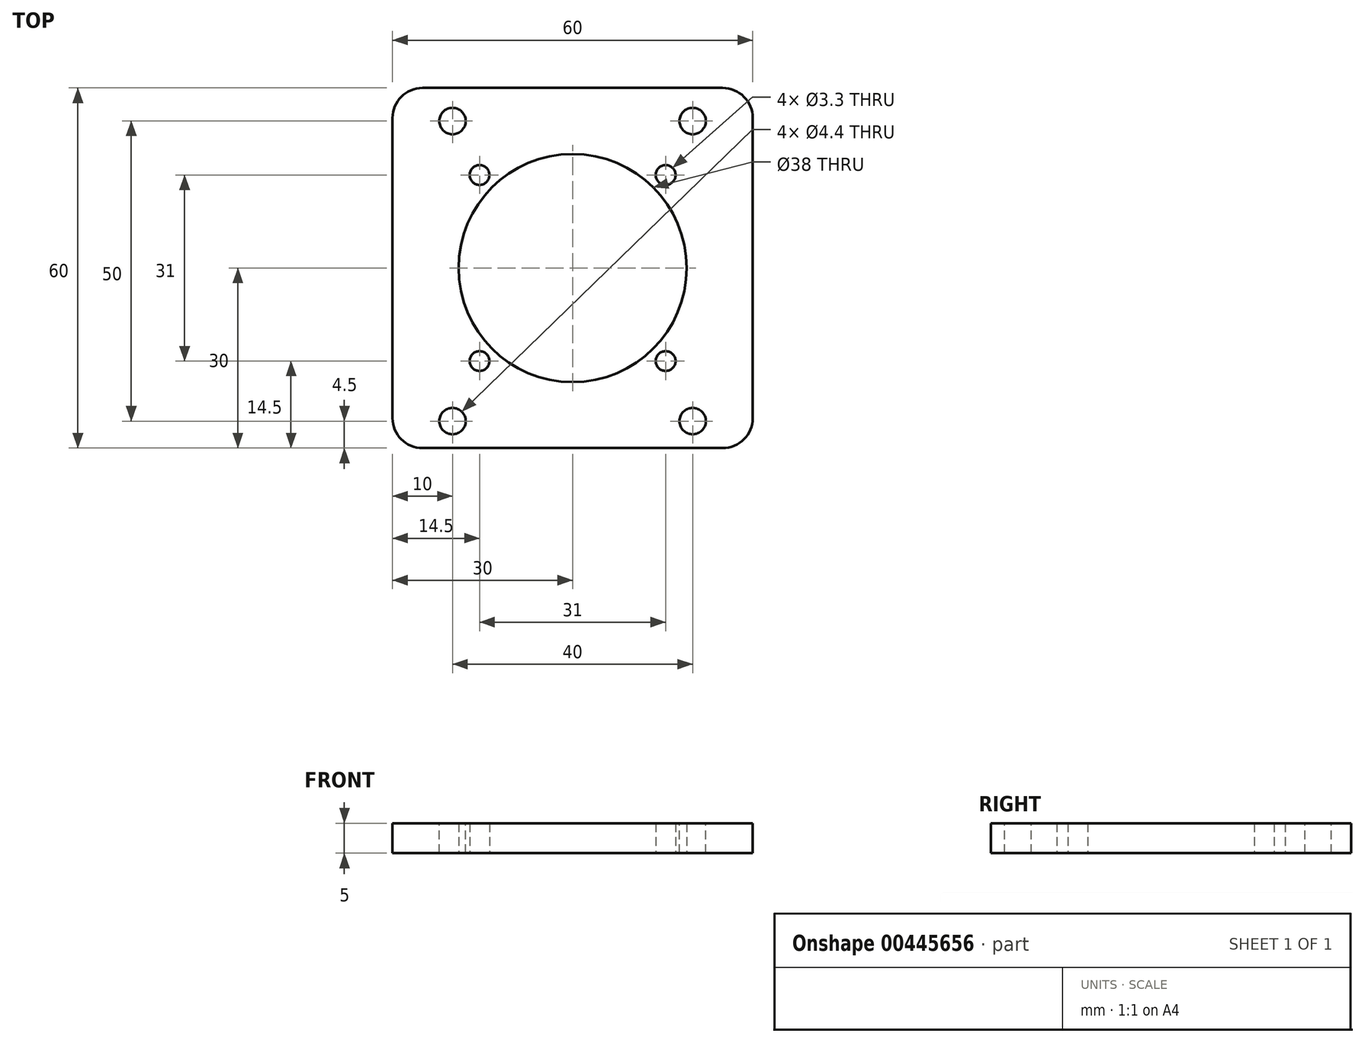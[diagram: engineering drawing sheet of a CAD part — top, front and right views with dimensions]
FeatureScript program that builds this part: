
annotation { "Feature Type Name" : "Feature", "Feature Type Description" : "" }
export const myFeature = defineFeature(function(context is Context, id is Id, definition is map)
    precondition{}
    {
        {
            var Q0;
            Q0=qCreatedBy(makeId("Top.planeOp"),FACE);
            var sketch = newSketch(context, id + "F0", { "sketchPlane" : qUnion([Q0])});
            skLineSegment(sketch, "E0.bottom", {"start": v(30, 30) * mm, "end": v(-30, 30) * mm});
            skLineSegment(sketch, "E0.top", {"start": v(30, -30) * mm, "end": v(-30, -30) * mm});
            skLineSegment(sketch, "E0.left", {"start": v(30, 30) * mm, "end": v(30, -30) * mm});
            skLineSegment(sketch, "E0.right", {"start": v(-30, 30) * mm, "end": v(-30, -30) * mm});
            skPoint(sketch, "E0.middle", {"position": v(0, 0) * mm});
            skCircle(sketch, "E1", {"center": v(0, 0) * mm, "radius": 19 * mm});
            skLineSegment(sketch, "E2.bottom", {"start": v(-15.5, 15.5) * mm, "end": v(15.5, 15.5) * mm, "construction": true});
            skLineSegment(sketch, "E2.top", {"start": v(-15.5, -15.5) * mm, "end": v(15.5, -15.5) * mm, "construction": true});
            skLineSegment(sketch, "E2.left", {"start": v(-15.5, 15.5) * mm, "end": v(-15.5, -15.5) * mm, "construction": true});
            skLineSegment(sketch, "E2.right", {"start": v(15.5, 15.5) * mm, "end": v(15.5, -15.5) * mm, "construction": true});
            skSolve(sketch);
        }
        {
            var Q0;
            Q0=qSketchRegion(id+"F0",true);
            extrude(context, id + "F1", {"entities" : qUnion([Q0]), "depth" : 5 * mm});
        }
        {
            var Q0;
            Q0=sQuery(id+"F0.wireOp",VERTEX,"E2.left.start");
            var Q1;
            Q1=sQuery(id+"F0.wireOp",VERTEX,"E2.right.start");
            var Q2;
            Q2=sQuery(id+"F0.wireOp",VERTEX,"E2.right.end");
            var Q3;
            Q3=sQuery(id+"F0.wireOp",VERTEX,"E2.left.end");
            var Q4;
            Q4=makeQuery(id+"F1.opExtrude","SWEPT_BODY",BODY,{"disambiguationData":[OSD([sQuery(id+"F0.wireOp",EDGE,"E0.bottom"),sQuery(id+"F0.wireOp",EDGE,"E0.top"),sQuery(id+"F0.wireOp",EDGE,"E0.left"),sQuery(id+"F0.wireOp",EDGE,"E0.right"),sQuery(id+"F0.wireOp",EDGE,"E1")])]});
            hole(context, id + "F2", {"style" : HoleStyle.SIMPLE, "endStyle" : HoleEndStyle.BLIND, "oppositeDirection" : true, "standardTappedOrClearance" : lookupTablePath({ "standard" : "ISO", "fit" : "Normal", "size" : "M3", "type" : "Clearance" }), "standardBlindInLast" : lookupTablePath({ "fit" : "Standard", "standard" : "ISO", "size" : "M3", "type" : "Clearance" }), "holeDiameter" : 3.3 * mm, "holeDepth" : 13.8 * mm, "tappedDepth" : 12 * mm, "tapClearance" : 3, "locations" : qUnion([Q0, Q1, Q2, Q3]), "scope" : qUnion([Q4])});
        }
        {
            var Q0;
            Q0=makeQuery(id+"F1.opExtrude","CAP_FACE",FACE,{"disambiguationData":[OSD([sQuery(id+"F0.wireOp",EDGE,"E0.bottom"),sQuery(id+"F0.wireOp",EDGE,"E0.top"),sQuery(id+"F0.wireOp",EDGE,"E0.left"),sQuery(id+"F0.wireOp",EDGE,"E0.right"),sQuery(id+"F0.wireOp",EDGE,"E1")])],"isStart":false});
            var sketch = newSketch(context, id + "F3", { "sketchPlane" : qUnion([Q0])});
            skPoint(sketch, "E3", {"position": v(-20, 24.5) * mm});
            skPoint(sketch, "E4.0.1.0", {"position": v(-20, -25.5) * mm});
            skPoint(sketch, "E4.1.0.0", {"position": v(20, 24.5) * mm});
            skPoint(sketch, "E4.1.1.0", {"position": v(20, -25.5) * mm});
            skLineSegment(sketch, "E4.direction1", {"start": v(-24, 20) * mm, "end": v(16, 20) * mm, "construction": true});
            skLineSegment(sketch, "E4.direction2", {"start": v(-24, 20) * mm, "end": v(-24, -30) * mm, "construction": true});
            skSolve(sketch);
        }
        {
            var Q0;
            Q0=sQuery(id+"F3.wireOp",VERTEX,"E3");
            var Q1;
            Q1=sQuery(id+"F3.wireOp",VERTEX,"E4.1.0.0");
            var Q2;
            Q2=sQuery(id+"F3.wireOp",VERTEX,"E4.1.1.0");
            var Q3;
            Q3=sQuery(id+"F3.wireOp",VERTEX,"E4.0.1.0");
            var Q4;
            Q4=makeQuery(id+"F1.opExtrude","SWEPT_BODY",BODY,{"disambiguationData":[OSD([sQuery(id+"F0.wireOp",EDGE,"E0.bottom"),sQuery(id+"F0.wireOp",EDGE,"E0.top"),sQuery(id+"F0.wireOp",EDGE,"E0.left"),sQuery(id+"F0.wireOp",EDGE,"E0.right"),sQuery(id+"F0.wireOp",EDGE,"E1")])]});
            hole(context, id + "F4", {"style" : HoleStyle.SIMPLE, "endStyle" : HoleEndStyle.BLIND, "standardTappedOrClearance" : lookupTablePath({ "standard" : "ISO", "fit" : "Normal", "size" : "M4", "type" : "Clearance" }), "standardBlindInLast" : lookupTablePath({ "fit" : "Standard", "standard" : "ISO", "size" : "M4", "type" : "Clearance" }), "holeDiameter" : 4.4 * mm, "holeDepth" : 13.8 * mm, "tappedDepth" : 12 * mm, "tapClearance" : 3, "locations" : qUnion([Q0, Q1, Q2, Q3]), "scope" : qUnion([Q4])});
        }
        {
            var Q0;
            Q0=makeQuery(id+"F1.opExtrude","SWEPT_EDGE",EDGE,{"disambiguationData":[OSD([sQuery(id+"F0.wireOp",EDGE,"E0.bottom"),sQuery(id+"F0.wireOp",EDGE,"E0.right")])]});
            var Q1;
            Q1=makeQuery(id+"F1.opExtrude","SWEPT_EDGE",EDGE,{"disambiguationData":[OSD([sQuery(id+"F0.wireOp",EDGE,"E0.bottom"),sQuery(id+"F0.wireOp",EDGE,"E0.left")])]});
            var Q2;
            Q2=makeQuery(id+"F1.opExtrude","SWEPT_EDGE",EDGE,{"disambiguationData":[OSD([sQuery(id+"F0.wireOp",EDGE,"E0.top"),sQuery(id+"F0.wireOp",EDGE,"E0.left")])]});
            var Q3;
            Q3=makeQuery(id+"F1.opExtrude","SWEPT_EDGE",EDGE,{"disambiguationData":[OSD([sQuery(id+"F0.wireOp",EDGE,"E0.top"),sQuery(id+"F0.wireOp",EDGE,"E0.right")])]});
            fillet(context, id + "F5", {"entities" : qUnion([Q0, Q1, Q2, Q3]), "radius" : 5 * mm, "tangentPropagation" : true, "allowEdgeOverflow" : false});
        }
    });
